# Revit family: Hand_Dryer-Automatic-Bobrick-Fino-B-7179
name_source: partatom
category: Specialty Equipment
revit_build: Autodesk Revit 2018 (Build: 20170223_1515(x64)
units: mm (PartAtom-declared; Revit-internal decimal feet)

## family parameters
Cut with Voids When Loaded = No
Host = Face
OmniClass Number = 23.40.20.21.14
OmniClass Title = Hand and Hair Dryers
Part Type = Normal
Room Calculation Point = No
Round Connector Dimension = Use Diameter
Shared = Yes

## types (2) — shared parameters
ADA Compliant = Yes
Assembly Code = C1030200
Default Elevation = 0"
Description = Fino Collection Surface Mounted Automatic Hand Dryer
Dry Time = Less than 12 seconds
Energy Consumption = 200 Watts
Finish = Stainless_Steel-Bobrick-Type_304-Satin_Finish
Height = 13 1/2"
Installation Type = Wall Mounted
Length = 11 3/4"
Manufacturer = Bobrick
Material = Stainless_Steel-Bobrick-Type_304-Satin_Finish
Model = B-7179
Motor Operation = 40,000 RPM
Motor Power = 24 Vdc
Mounting Base Thickness = 1/16"
Mounting Height From Floor = 40"
Price = Prices may vary. Please consult Manufacturer Representative for most up-to-date price list.
URL = https://www.bobrick.com
Universal Voltage = 110V–240V, 0.8–1.9 AMP, 50/60 Hz, 202–213 Watts
Warranty Information = 5-year limited warranty
Width = 4"
Wiring Hole Diameter = 3/4"

## per-type parameters (varying)
| type | Voltage |
| B-7179-(115 Volts) | 115 Volts |
| B-7179-(208–240 Volts) | 208–240 Volts |

## geometry (parser evidence)
native form markers: Sweep x3
no freeform markers — native parametric forms only
